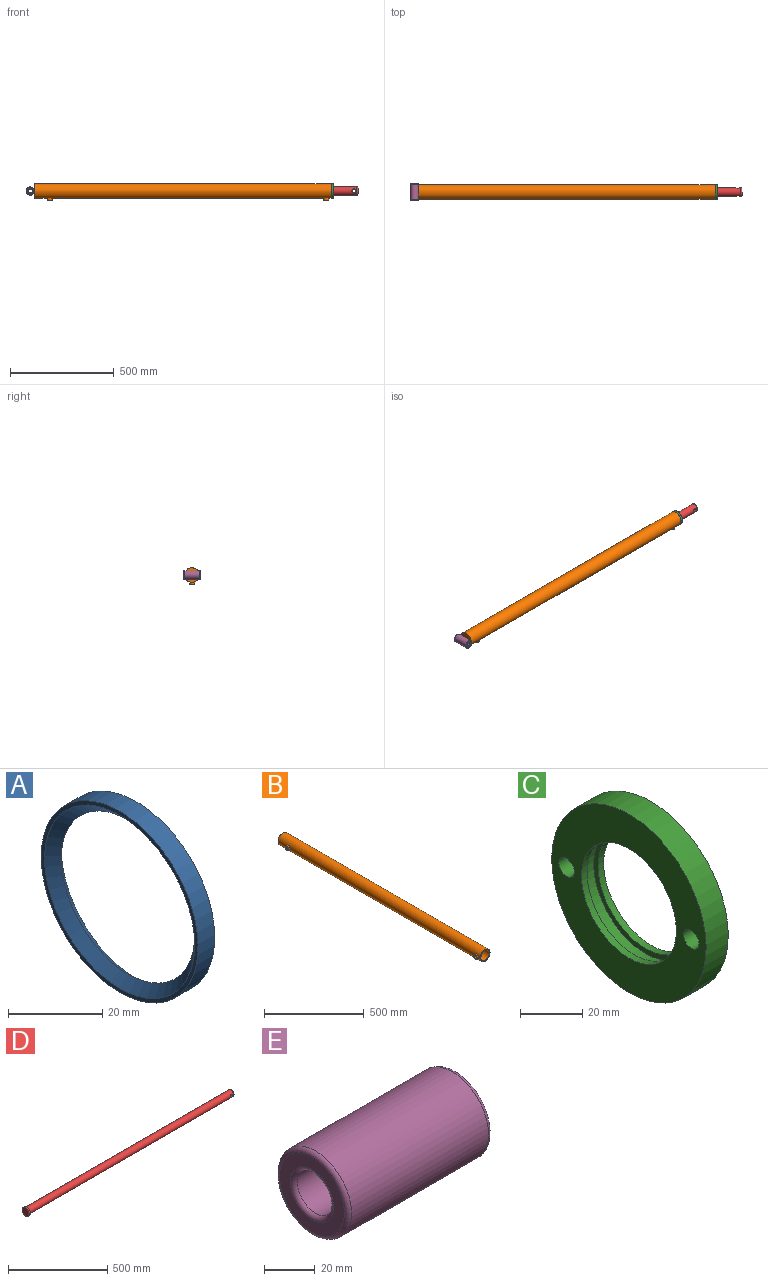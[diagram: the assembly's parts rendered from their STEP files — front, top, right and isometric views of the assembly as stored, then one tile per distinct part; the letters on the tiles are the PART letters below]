
ASSEMBLY  parts=5 mates=4
PART A: 5 faces, bbox 5x47x47 mm
  f0: cylinder r=23.5mm len=47mm, axis (-1,0,0), area 738.3mm2, adj f1,f2
  f1: plane 47x47mm, normal (1,0,0), area 144.5mm2, adj f0,f3
  f2: plane 47x47mm, normal (-1,0,0), area 144.5mm2, adj f0,f4
  f3: cone r=20mm half-angle=45deg, axis (1,0,0), area 472.1mm2, adj f1,f4
  f4: cone r=22.5mm half-angle=45deg, axis (-1,0,0), area 472.1mm2, adj f2,f3
PART B: 23 faces, bbox 79.7x1430x70 mm
  f0: cylinder r=30mm len=16mm, axis (0,-1,0), area 24.8mm2, adj f17,f21
  f1: cylinder r=35mm len=16mm, axis (0,1,0), area 24.7mm2, adj f19,f21
  f2: cylinder r=35mm len=1430mm, axis (0,1,0), area 313551.8mm2, adj f4,f5,f11,f18
  f3: cylinder r=30mm len=1420mm, axis (0,-1,0), area 266740.3mm2, adj f4,f6,f7,f15
  f4: plane 70x70mm, normal (0,-1,0), area 1021mm2, adj f2,f3
  f5: plane 70x70mm, normal (0,1,0), area 3848.5mm2, adj f2
  f6: plane 60x60mm, normal (0,-1,0), area 2827.4mm2, adj f3
  f7: cylinder r=12mm len=24mm, axis (1,0,0), area 283.8mm2, adj f3,f8
  f8: plane 24x24mm, normal (1,0,0), area 251.3mm2, adj f7,f9
  f9: cylinder r=8mm len=16mm, axis (1,0,0), area 224.1mm2, adj f8,f10
  f10: cylinder r=30mm len=16mm, axis (0,-1,0), area 24.8mm2, adj f9,f22
  f11: cylinder r=12mm len=24mm, axis (1,0,0), area 812mm2, adj f2,f13
  f12: cylinder r=8mm len=16mm, axis (1,0,0), area 511.6mm2, adj f13,f14
  f13: plane 24x24mm, normal (-1,0,0), area 251.3mm2, adj f11,f12
  f14: cylinder r=35mm len=16mm, axis (0,1,0), area 24.7mm2, adj f12,f22
  f15: cylinder r=12mm len=24mm, axis (1,0,0), area 283.5mm2, adj f3,f16
  f16: plane 24x24mm, normal (1,0,0), area 251.3mm2, adj f15,f17
  f17: cylinder r=8mm len=16mm, axis (1,0,0), area 224.2mm2, adj f0,f16
  f18: cylinder r=12mm len=24mm, axis (1,0,0), area 811.8mm2, adj f2,f20
  f19: cylinder r=8mm len=16mm, axis (1,0,0), area 511.6mm2, adj f1,f20
  f20: plane 24x24mm, normal (-1,0,0), area 251.3mm2, adj f18,f19
  f21: cylinder r=7.5mm len=15mm, axis (1,0,0), area 252.2mm2, adj f0,f1
  f22: cylinder r=7.5mm len=15mm, axis (1,0,0), area 252.3mm2, adj f10,f14
PART C: 12 faces, bbox 10x70x70 mm
  f0: plane 70x70mm, normal (-1,0,0), area 2319.3mm2, adj f1,f3,f8,f10
  f1: cylinder r=21.5mm len=43mm, axis (-1,0,0), area 337.7mm2, adj f0,f7
  f2: cylinder r=21.5mm len=43mm, axis (-1,0,0), area 337.7mm2, adj f4,f6
  f3: cylinder r=35mm len=70mm, axis (-1,0,0), area 2199.1mm2, adj f0,f4
  f4: plane 70x70mm, normal (1,0,0), area 2396.2mm2, adj f2,f3
  f5: cylinder r=23.5mm len=47mm, axis (-1,0,0), area 738.3mm2, adj f6,f7
  f6: plane 47x47mm, normal (-1,0,0), area 282.7mm2, adj f2,f5
  f7: plane 47x47mm, normal (1,0,0), area 282.7mm2, adj f1,f5
  f8: cylinder r=3.5mm len=8mm, axis (-1,0,0), area 175.9mm2, adj f0,f9
  f9: plane 7x7mm, normal (-1,0,0), area 38.5mm2, adj f8
  f10: cylinder r=3.5mm len=8mm, axis (-1,0,0), area 175.9mm2, adj f0,f11
  f11: plane 7x7mm, normal (-1,0,0), area 38.5mm2, adj f10
PART D: 7 faces, bbox 1470x50x50 mm
  f0: cylinder r=25mm len=50mm, axis (-1,0,0), area 1570.8mm2, adj f1,f3
  f1: plane 50x50mm, normal (-1,0,0), area 1963.5mm2, adj f0
  f2: cylinder r=20mm len=1455mm, axis (1,0,0), area 182190mm2, adj f3,f5,f6
  f3: plane 50x50mm, normal (1,0,0), area 706.9mm2, adj f0,f2
  f4: plane 30x30mm, normal (1,0,0), area 706.9mm2, adj f5
  f5: torus R=15mm, axis (1,0,0), area 897.3mm2, adj f2,f4
  f6: cylinder r=10mm len=40mm, axis (0,-1,0), area 2348mm2, adj f2
PART E: 9 faces, bbox 80x43.3x43.3 mm
  f0: cylinder r=10mm len=76mm, axis (-1,0,0), area 4717mm2, adj f4,f6,f8
  f1: cylinder r=20mm len=76mm, axis (-1,0,0), area 9493.6mm2, adj f5,f7,f8
  f2: plane 36x36mm, normal (1,0,0), area 565.5mm2, adj f6,f7
  f3: plane 36x36mm, normal (-1,0,0), area 565.5mm2, adj f4,f5
  f4: torus R=12mm, axis (1,0,0), area 211.7mm2, adj f0,f3
  f5: torus R=18mm, axis (1,0,0), area 380.4mm2, adj f1,f3
  f6: torus R=12mm, axis (1,0,0), area 211.7mm2, adj f0,f2
  f7: torus R=18mm, axis (1,0,0), area 380.4mm2, adj f1,f2
  f8: cylinder r=4.25mm len=10.95mm, axis (0,-1,0), area 273.5mm2, adj f0,f1
PLACE A rot(axis=(0,1,0),180deg) t=(-422.02,-261.61,61.71)mm
PLACE B rot(axis=(0.58,-0.58,0.58),120deg) t=(-1859.52,-261.61,61.71)mm
PLACE C rot(axis=(0,1,0),180deg) t=(-419.52,-261.61,61.71)mm
PLACE D t=(-1769.52,-261.61,61.71)mm
PLACE E rot(axis=(0,0,-1),90deg) t=(-1880.04,-221.03,61.42)mm
MATE fastened C.f5 <-> A.f0  axis (1,0,0) through (-424.52,-261.61,61.71)mm
MATE slider D.f2 <-> C.f1  axis (1,0,0) through (-299.52,-261.61,61.71)mm
MATE fastened B.f0 <-> C.f1  axis (1,0,0) through (-429.52,-261.61,61.71)mm
MATE fastened E.f8 <-> B.f1  axis (-1,0,0) through (-1865.52,-261.03,61.42)mm
